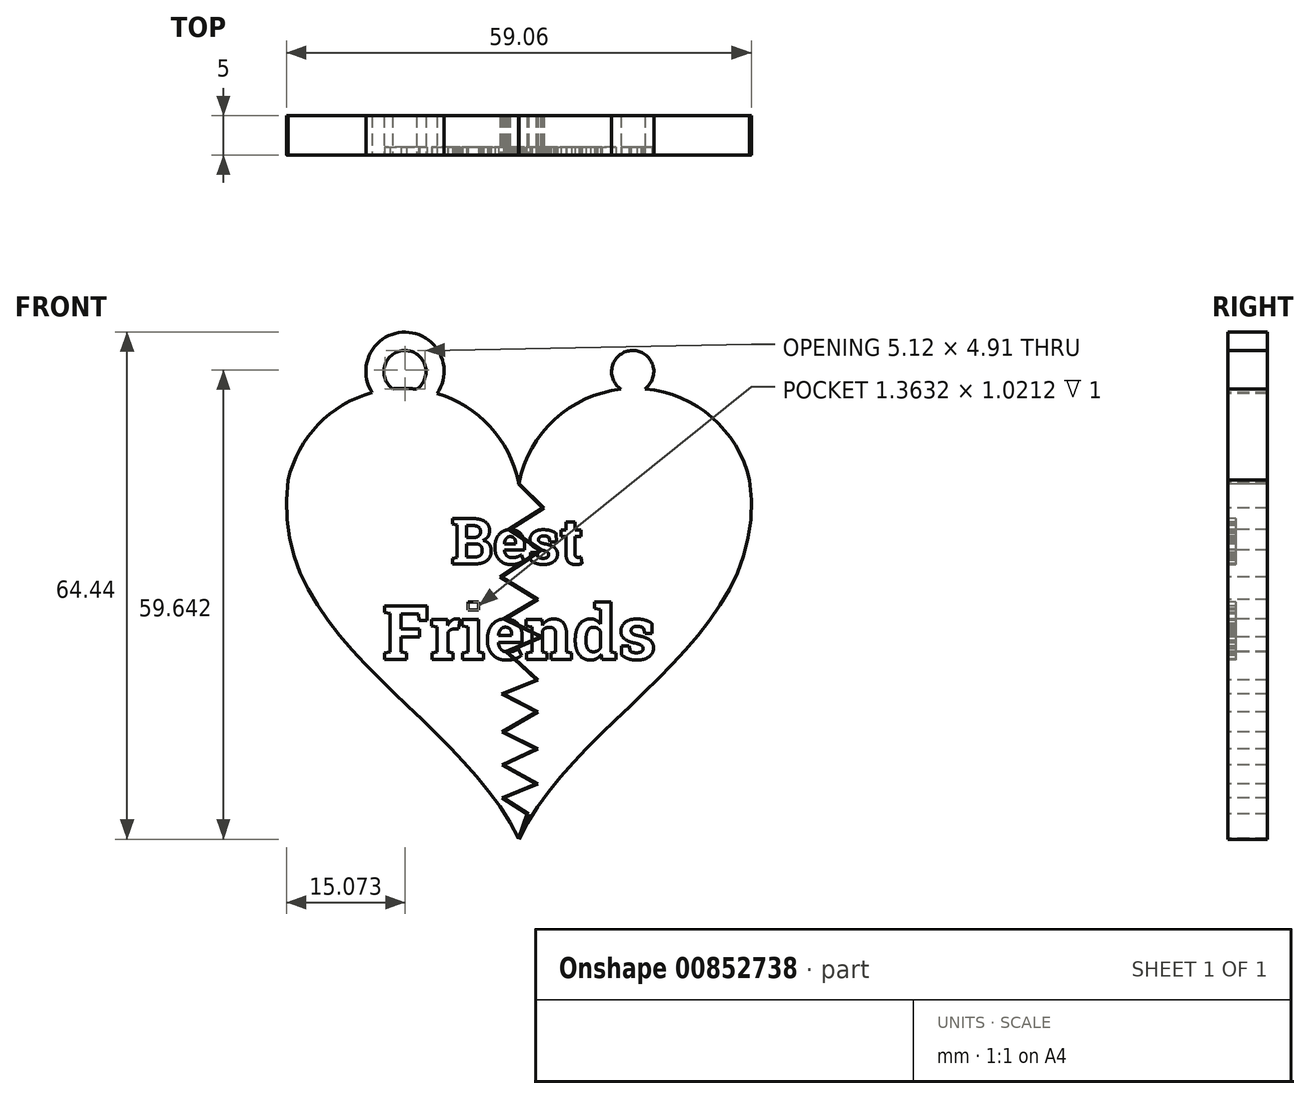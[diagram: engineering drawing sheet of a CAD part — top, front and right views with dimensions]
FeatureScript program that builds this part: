
annotation { "Feature Type Name" : "Feature", "Feature Type Description" : "" }
export const myFeature = defineFeature(function(context is Context, id is Id, definition is map)
    precondition{}
    {
        {
            var Q0;
            Q0=qCreatedBy(makeId("Front.planeOp"),FACE);
            var sketch = newSketch(context, id + "F0", { "sketchPlane" : qUnion([Q0])});
            skLineSegment(sketch, "E0", {"start": v(0, 34.53) * mm, "end": v(0, -38.99) * mm, "construction": true});
            skArc(sketch, "E1", {"start": v(0, 19.83) * mm, "mid": v(-14.47, 31.88) * mm, "end": v(-29.3, 20.27) * mm});
            skFitSpline(sketch, "E2", {"points": [v(-29.3, 20.27) * mm, v(0, -25.4) * mm], "startDerivative": vector(-8.69, -60.81) * mm, "endDerivative": vector(23.06, -48.79) * mm});
            skArc(sketch, "E3.MirrorCS", {"start": v(0, 19.83) * mm, "mid": v(14.47, 31.88) * mm, "end": v(29.3, 20.27) * mm});
            skFitSpline(sketch, "E4.MirrorCS", {"points": [v(29.3, 20.27) * mm, v(0, -25.4) * mm], "startDerivative": vector(8.69, -60.81) * mm, "endDerivative": vector(-23.06, -48.79) * mm});
            skSolve(sketch);
        }
        {
            var Q0;
            Q0=makeQuery(id+"F0.imprint","IMPRINT",FACE,{"disambiguationData":[TD([[makeQuery(id+"F0.imprint","IMPRINT",EDGE,{"derivedFrom":sQuery(id+"F0.wireOp",EDGE,"E1")}),1.0]])]});
            extrude(context, id + "F1", {"entities" : qUnion([Q0]), "depth" : 5 * mm, "offsetDistance" : 25 * mm});
        }
        {
            var Q0;
            Q0=makeQuery(id+"F1.opExtrude","CAP_FACE",FACE,{"disambiguationData":[OSD([sQuery(id+"F0.wireOp",EDGE,"E1"),sQuery(id+"F0.wireOp",EDGE,"E2"),sQuery(id+"F0.wireOp",EDGE,"E3.MirrorCS"),sQuery(id+"F0.wireOp",EDGE,"E4.MirrorCS")])],"isStart":false});
            var sketch = newSketch(context, id + "F2", { "sketchPlane" : qUnion([Q0])});
            skText(sketch, "E5", { "text": "Best", "fontName": "RobotoSlab-Bold.ttf"});
            skText(sketch, "E6", { "text": "Friends", "fontName": "RobotoSlab-Bold.ttf"});
            const initialGuessF2  = {"E5": [-0.00865, 0.00959, 1, 0, 0.00583], "E6": [-0.01731, -0.00254, 1, 0, 0.00688]};
            skSetInitialGuess(sketch, initialGuessF2);
            skSolve(sketch);
        }
        {
            var Q0;
            Q0=qSketchRegion(id+"F2",true);
            extrude(context, id + "F3", {"entities" : qUnion([Q0]), "operationType" : NewBodyOperationType.REMOVE, "oppositeDirection" : true, "depth" : 1 * mm, "offsetDistance" : 25 * mm});
        }
        {
            var Q0;
            {var subQ0=sQuery(id+"F0.wireOp",EDGE,"E3.MirrorCS");var subQ1=sQuery(id+"F0.wireOp",EDGE,"E1");var subQ2=sQuery(id+"F0.wireOp",EDGE,"E4.MirrorCS");var subQ3=sQuery(id+"F0.wireOp",EDGE,"E2");Q0=makeQuery(id+"F3.boolean.opBoolean","SPLIT",FACE,{"disambiguationData":[TD([makeQuery(id+"F1.opExtrude","SWEPT_FACE",FACE,{"disambiguationData":[OSD([subQ1])]})])],"derivedFrom":makeQuery(id+"F1.opExtrude","CAP_FACE",FACE,{"disambiguationData":[OSD([subQ1,subQ3,subQ0,subQ2])],"isStart":false})});}
            var sketch = newSketch(context, id + "F4", { "sketchPlane" : qUnion([Q0])});
            skLineSegment(sketch, "E7", {"start": v(0, 19.83) * mm, "end": v(3.2, 16.7) * mm});
            skLineSegment(sketch, "E8", {"start": v(3.2, 16.7) * mm, "end": v(-1.1, 13.94) * mm});
            skLineSegment(sketch, "E9", {"start": v(-1.1, 13.94) * mm, "end": v(2.92, 11.34) * mm});
            skLineSegment(sketch, "E10", {"start": v(2.92, 11.34) * mm, "end": v(-2.2, 7.93) * mm});
            skLineSegment(sketch, "E11", {"start": v(-2.2, 7.93) * mm, "end": v(2.42, 5.1) * mm});
            skLineSegment(sketch, "E12", {"start": v(2.42, 5.1) * mm, "end": v(-1.72, 2.6) * mm});
            skLineSegment(sketch, "E13", {"start": v(-1.72, 2.6) * mm, "end": v(3.02, 0.32) * mm});
            skLineSegment(sketch, "E14", {"start": v(3.02, 0.32) * mm, "end": v(-1.45, -1.6) * mm});
            skLineSegment(sketch, "E15", {"start": v(-1.45, -1.6) * mm, "end": v(2.42, -5.16) * mm});
            skLineSegment(sketch, "E16", {"start": v(2.42, -5.16) * mm, "end": v(-1.94, -6.91) * mm});
            skLineSegment(sketch, "E17", {"start": v(-1.94, -6.91) * mm, "end": v(2.42, -9.2) * mm});
            skLineSegment(sketch, "E18", {"start": v(2.42, -9.2) * mm, "end": v(-1.94, -11.77) * mm});
            skLineSegment(sketch, "E19", {"start": v(-1.94, -11.77) * mm, "end": v(2.42, -13.93) * mm});
            skLineSegment(sketch, "E20", {"start": v(2.42, -13.93) * mm, "end": v(-1.94, -15.95) * mm});
            skLineSegment(sketch, "E21", {"start": v(-1.94, -15.95) * mm, "end": v(2.42, -18.38) * mm});
            skLineSegment(sketch, "E22", {"start": v(2.42, -18.38) * mm, "end": v(-1.94, -20.14) * mm});
            skPoint(sketch, "E23.end.orphan", {"position": v(2.42, -21.2) * mm});
            skLineSegment(sketch, "E24", {"start": v(-1.94, -20.14) * mm, "end": v(1.08, -22.1) * mm});
            skArc(sketch, "E25", {"start": v(-12.98, 31.79) * mm, "mid": v(-14.43, 36.7) * mm, "end": v(-16.01, 31.83) * mm});
            skPoint(sketch, "E25.centerSnap0", {"position": v(-14.47, 31.88) * mm});
            skArc(sketch, "E26", {"start": v(-10.37, 31.25) * mm, "mid": v(-14.4, 39.04) * mm, "end": v(-18.63, 31.36) * mm});
            skArc(sketch, "E27.0", {"start": v(0, 19.83) * mm, "mid": v(-3.6, 26.97) * mm, "end": v(-10.37, 31.25) * mm});
            skArc(sketch, "E28.trimOffspring", {"start": v(-12.98, 31.79) * mm, "mid": v(-14.5, 31.88) * mm, "end": v(-16.01, 31.83) * mm});
            skArc(sketch, "E29.trimOffspring", {"start": v(-18.63, 31.36) * mm, "mid": v(-25.5, 27.29) * mm, "end": v(-29.3, 20.27) * mm});
            skArc(sketch, "E30.MirrorCS", {"start": v(12.98, 31.79) * mm, "mid": v(14.43, 36.7) * mm, "end": v(16.01, 31.83) * mm});
            skArc(sketch, "E31.MirrorCS", {"start": v(10.37, 31.25) * mm, "mid": v(14.4, 39.04) * mm, "end": v(18.63, 31.36) * mm});
            skLineSegment(sketch, "E32.0", {"start": v(-2.15, -20.12) * mm, "end": v(1.03, -22.19) * mm});
            skLineSegment(sketch, "E32.1", {"start": v(2.2, -18.37) * mm, "end": v(-2.15, -20.12) * mm});
            skLineSegment(sketch, "E32.2", {"start": v(-2.16, -15.95) * mm, "end": v(2.2, -18.37) * mm});
            skLineSegment(sketch, "E32.3", {"start": v(2.2, -13.93) * mm, "end": v(-2.16, -15.95) * mm});
            skLineSegment(sketch, "E32.4", {"start": v(-2.15, -11.78) * mm, "end": v(2.2, -13.93) * mm});
            skLineSegment(sketch, "E32.5", {"start": v(2.22, -9.21) * mm, "end": v(-2.15, -11.78) * mm});
            skLineSegment(sketch, "E32.6", {"start": v(-2.17, -6.9) * mm, "end": v(2.22, -9.21) * mm});
            skLineSegment(sketch, "E32.7", {"start": v(2.74, 11.33) * mm, "end": v(-2.4, 7.93) * mm});
            skLineSegment(sketch, "E32.8", {"start": v(-1.29, 13.94) * mm, "end": v(2.74, 11.33) * mm});
            skLineSegment(sketch, "E32.9", {"start": v(3.03, 16.72) * mm, "end": v(-1.29, 13.94) * mm});
            skLineSegment(sketch, "E32.10", {"start": v(-0.07, 19.75) * mm, "end": v(3.03, 16.72) * mm});
            skLineSegment(sketch, "E32.11", {"start": v(-2.4, 7.93) * mm, "end": v(2.23, 5.1) * mm});
            skLineSegment(sketch, "E32.12", {"start": v(2.23, 5.1) * mm, "end": v(-1.93, 2.6) * mm});
            skLineSegment(sketch, "E32.13", {"start": v(-1.93, 2.6) * mm, "end": v(2.78, 0.32) * mm});
            skLineSegment(sketch, "E32.14", {"start": v(2.78, 0.32) * mm, "end": v(-1.63, -1.56) * mm});
            skLineSegment(sketch, "E32.15", {"start": v(-1.63, -1.56) * mm, "end": v(2.24, -5.13) * mm});
            skLineSegment(sketch, "E32.16", {"start": v(2.24, -5.13) * mm, "end": v(-2.17, -6.9) * mm});
            skLineSegment(sketch, "E33", {"start": v(1.03, -22.19) * mm, "end": v(-0.04, -25.31) * mm});
            skLineSegment(sketch, "E34", {"start": v(1.08, -22.1) * mm, "end": v(1.21, -22.19) * mm});
            skLineSegment(sketch, "E35", {"start": v(1.21, -22.19) * mm, "end": v(0, -25.4) * mm});
            skLineSegment(sketch, "E36", {"start": v(0, -25.4) * mm, "end": v(0, -25.36) * mm});
            skLineSegment(sketch, "E37", {"start": v(-0.07, 19.75) * mm, "end": v(-0.04, 20) * mm});
            skSolve(sketch);
        }
        {
            var Q0;
            {var subQ6=sQuery(id+"F4.wireOp",EDGE,"E16");Q0=makeQuery(id+"F4.imprint","IMPRINT",FACE,{"disambiguationData":[TD([[makeQuery(id+"F4.imprint","IMPRINT",EDGE,{"derivedFrom":subQ6}),-1.0]])]});}
            var Q1;
            {var subQ1=makeQuery(id+"F3.boolean.opBoolean","COPY",EDGE,{"derivedFrom":makeQuery(id+"F3.opExtrude","CAP_EDGE",EDGE,{"disambiguationData":[OSD([sQuery(id+"F2.wireOp",EDGE,"E6.sketch_text.stroke-62")])],"isStart":true})});var subQ5=sQuery(id+"F4.wireOp",EDGE,"E32.15");var subQ6=makeQuery(id+"F4.imprint","INTERSECT",VERTEX,{"derivedFrom":[subQ1,subQ5]});Q1=makeQuery(id+"F4.imprint","IMPRINT",FACE,{"disambiguationData":[TD([[makeQuery(id+"F4.imprint","IMPRINT",EDGE,{"disambiguationData":[TD([[subQ6,-1.0]])],"derivedFrom":subQ5}),1.0]])]});}
            var Q2;
            {var subQ3=sQuery(id+"F4.wireOp",EDGE,"E32.15");var subQ5=sQuery(id+"F4.wireOp",EDGE,"E32.14");var subQ6=makeQuery(id+"F4.imprint","INTERSECT",VERTEX,{"derivedFrom":[subQ5,subQ3]});Q2=makeQuery(id+"F4.imprint","IMPRINT",FACE,{"disambiguationData":[TD([[makeQuery(id+"F4.imprint","IMPRINT",EDGE,{"disambiguationData":[TD([[subQ6,1.0]])],"derivedFrom":subQ5}),1.0]])]});}
            var Q3;
            {var subQ0=sQuery(id+"F4.wireOp",EDGE,"E32.14");var subQ1=sQuery(id+"F4.wireOp",EDGE,"E32.13");var subQ2=makeQuery(id+"F4.imprint","INTERSECT",VERTEX,{"derivedFrom":[subQ1,subQ0]});Q3=makeQuery(id+"F4.imprint","IMPRINT",FACE,{"disambiguationData":[TD([[makeQuery(id+"F4.imprint","IMPRINT",EDGE,{"disambiguationData":[TD([[subQ2,1.0]])],"derivedFrom":subQ1}),1.0]])]});}
            var Q4;
            {var subQ0=sQuery(id+"F4.wireOp",EDGE,"E13");var subQ1=makeQuery(id+"F3.boolean.opBoolean","COPY",EDGE,{"derivedFrom":makeQuery(id+"F3.opExtrude","CAP_EDGE",EDGE,{"disambiguationData":[OSD([sQuery(id+"F2.wireOp",EDGE,"E6.sketch_text.stroke-57")])],"isStart":true})});var subQ2=makeQuery(id+"F4.imprint","INTERSECT",VERTEX,{"derivedFrom":[subQ1,subQ0]});Q4=makeQuery(id+"F4.imprint","IMPRINT",FACE,{"disambiguationData":[TD([[makeQuery(id+"F4.imprint","IMPRINT",EDGE,{"disambiguationData":[TD([[subQ2,-1.0]])],"derivedFrom":subQ0}),-1.0]])]});}
            var Q5;
            {var subQ0=sQuery(id+"F4.wireOp",EDGE,"E32.13");var subQ1=sQuery(id+"F4.wireOp",EDGE,"E32.12");var subQ2=makeQuery(id+"F4.imprint","INTERSECT",VERTEX,{"derivedFrom":[subQ1,subQ0]});Q5=makeQuery(id+"F4.imprint","IMPRINT",FACE,{"disambiguationData":[TD([[makeQuery(id+"F4.imprint","IMPRINT",EDGE,{"disambiguationData":[TD([[subQ2,1.0]])],"derivedFrom":subQ1}),1.0]])]});}
            var Q6;
            {var subQ4=sQuery(id+"F4.wireOp",EDGE,"E11");Q6=makeQuery(id+"F4.imprint","IMPRINT",FACE,{"disambiguationData":[TD([[makeQuery(id+"F4.imprint","IMPRINT",EDGE,{"derivedFrom":subQ4}),-1.0]])]});}
            var Q7;
            {var subQ0=sQuery(id+"F4.wireOp",EDGE,"E10");var subQ1=makeQuery(id+"F3.boolean.opBoolean","COPY",EDGE,{"derivedFrom":makeQuery(id+"F3.opExtrude","CAP_EDGE",EDGE,{"disambiguationData":[OSD([sQuery(id+"F2.wireOp",EDGE,"E5.sketch_text.stroke-70")])],"isStart":true})});var subQ2=makeQuery(id+"F4.imprint","INTERSECT",VERTEX,{"derivedFrom":[subQ1,subQ0]});Q7=makeQuery(id+"F4.imprint","IMPRINT",FACE,{"disambiguationData":[TD([[makeQuery(id+"F4.imprint","IMPRINT",EDGE,{"disambiguationData":[TD([[subQ2,-1.0]])],"derivedFrom":subQ0}),-1.0]])]});}
            var Q8;
            {var subQ3=sQuery(id+"F4.wireOp",EDGE,"E32.7");var subQ5=sQuery(id+"F4.wireOp",EDGE,"E32.8");var subQ6=makeQuery(id+"F4.imprint","INTERSECT",VERTEX,{"derivedFrom":[subQ3,subQ5]});Q8=makeQuery(id+"F4.imprint","IMPRINT",FACE,{"disambiguationData":[TD([[makeQuery(id+"F4.imprint","IMPRINT",EDGE,{"disambiguationData":[TD([[subQ6,-1.0]])],"derivedFrom":subQ3}),1.0]])]});}
            var Q9;
            {var subQ3=makeQuery(id+"F3.boolean.opBoolean","COPY",EDGE,{"derivedFrom":makeQuery(id+"F3.opExtrude","CAP_EDGE",EDGE,{"disambiguationData":[OSD([sQuery(id+"F2.wireOp",EDGE,"E5.sketch_text.stroke-78")])],"isStart":true})});var subQ5=sQuery(id+"F4.wireOp",EDGE,"E32.8");var subQ6=makeQuery(id+"F4.imprint","INTERSECT",VERTEX,{"derivedFrom":[subQ3,subQ5]});Q9=makeQuery(id+"F4.imprint","IMPRINT",FACE,{"disambiguationData":[TD([[makeQuery(id+"F4.imprint","IMPRINT",EDGE,{"disambiguationData":[TD([[subQ6,-1.0]])],"derivedFrom":subQ5}),1.0]])]});}
            var Q10;
            {var subQ0=sQuery(id+"F4.wireOp",EDGE,"E9");var subQ1=makeQuery(id+"F3.boolean.opBoolean","COPY",EDGE,{"derivedFrom":makeQuery(id+"F3.opExtrude","CAP_EDGE",EDGE,{"disambiguationData":[OSD([sQuery(id+"F2.wireOp",EDGE,"E5.sketch_text.stroke-36")])],"isStart":true})});var subQ2=makeQuery(id+"F4.imprint","INTERSECT",VERTEX,{"derivedFrom":[subQ1,subQ0]});Q10=makeQuery(id+"F4.imprint","IMPRINT",FACE,{"disambiguationData":[TD([[makeQuery(id+"F4.imprint","IMPRINT",EDGE,{"disambiguationData":[TD([[subQ2,-1.0]])],"derivedFrom":subQ0}),-1.0]])]});}
            var Q11;
            {var subQ1=makeQuery(id+"F3.boolean.opBoolean","COPY",EDGE,{"derivedFrom":makeQuery(id+"F3.opExtrude","CAP_EDGE",EDGE,{"disambiguationData":[OSD([sQuery(id+"F2.wireOp",EDGE,"E5.sketch_text.stroke-34")])],"isStart":true})});var subQ5=sQuery(id+"F4.wireOp",EDGE,"E32.8");var subQ6=makeQuery(id+"F4.imprint","INTERSECT",VERTEX,{"derivedFrom":[subQ1,subQ5]});Q11=makeQuery(id+"F4.imprint","IMPRINT",FACE,{"disambiguationData":[TD([[makeQuery(id+"F4.imprint","IMPRINT",EDGE,{"disambiguationData":[TD([[subQ6,-1.0]])],"derivedFrom":subQ5}),1.0]])]});}
            var Q12;
            {var subQ6=sQuery(id+"F4.wireOp",EDGE,"E7");Q12=makeQuery(id+"F4.imprint","IMPRINT",FACE,{"disambiguationData":[TD([[makeQuery(id+"F4.imprint","IMPRINT",EDGE,{"derivedFrom":subQ6}),-1.0]])]});}
            extrude(context, id + "F5", {"entities" : qUnion([Q0, Q1, Q2, Q3, Q4, Q5, Q6, Q7, Q8, Q9, Q10, Q11, Q12]), "operationType" : NewBodyOperationType.REMOVE, "oppositeDirection" : true, "depth" : 25 * mm, "offsetDistance" : 25 * mm});
        }
        {
            var Q0;
            {var subQ0=sQuery(id+"F4.wireOp",EDGE,"E25");Q0=makeQuery(id+"F4.imprint","IMPRINT",FACE,{"disambiguationData":[TD([[makeQuery(id+"F4.imprint","IMPRINT",EDGE,{"derivedFrom":subQ0}),-1.0]])]});}
            var Q1;
            {var subQ0=sQuery(id+"F4.wireOp",EDGE,"E30.MirrorCS");Q1=makeQuery(id+"F4.imprint","IMPRINT",FACE,{"disambiguationData":[TD([[makeQuery(id+"F4.imprint","IMPRINT",EDGE,{"derivedFrom":subQ0}),1.0]])]});}
            extrude(context, id + "F6", {"entities" : qUnion([Q0, Q1]), "operationType" : NewBodyOperationType.ADD, "oppositeDirection" : true, "depth" : 5 * mm, "offsetDistance" : 25 * mm});
        }
    });
